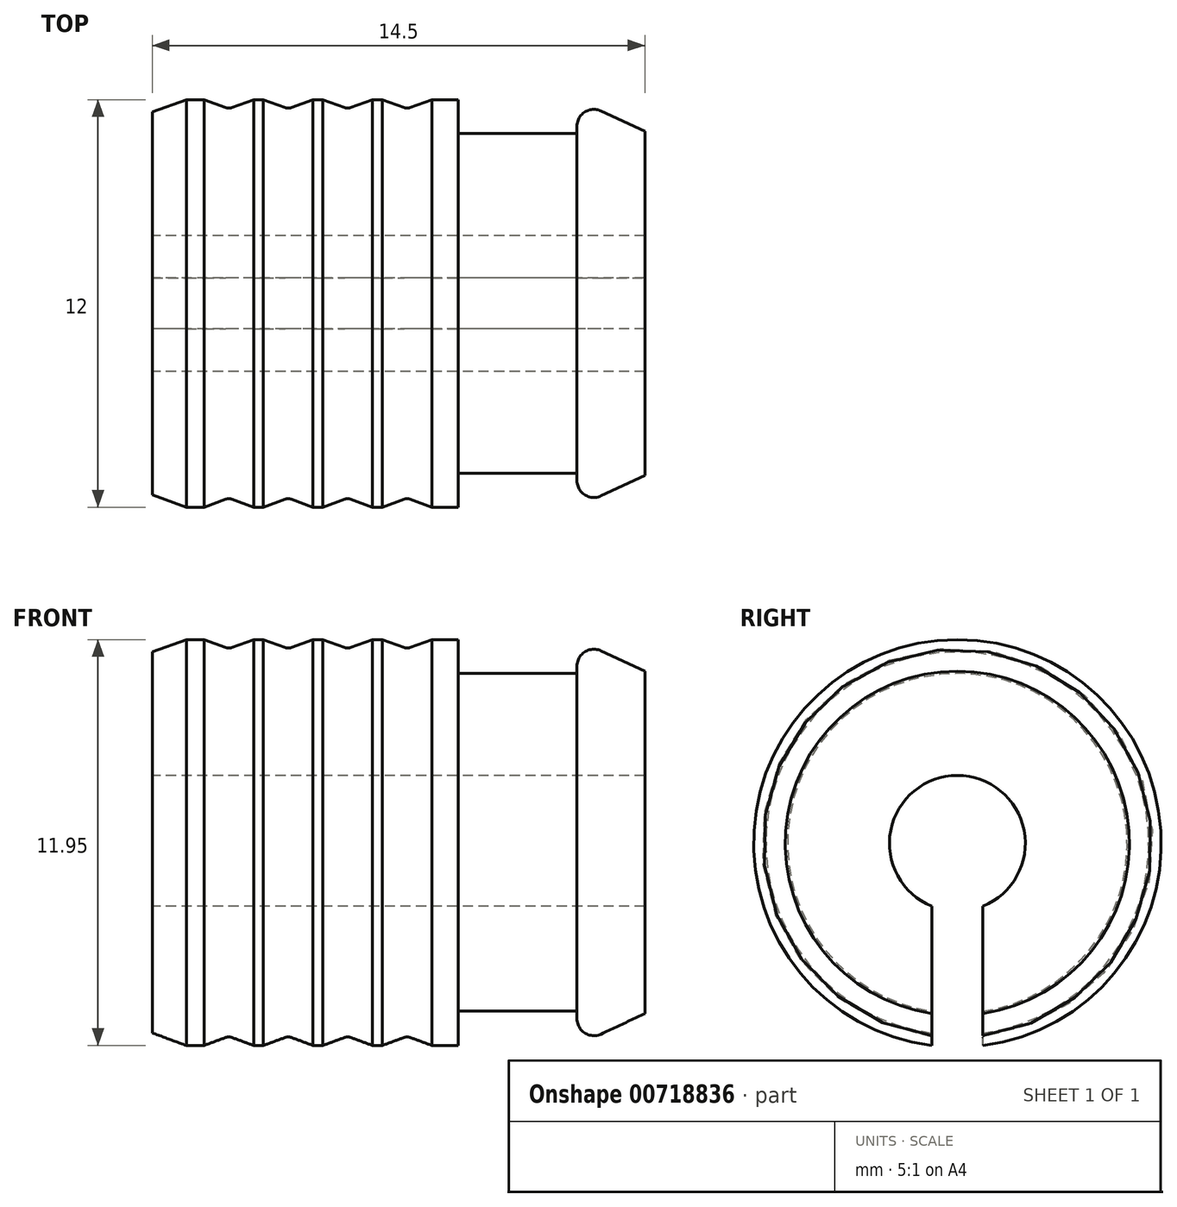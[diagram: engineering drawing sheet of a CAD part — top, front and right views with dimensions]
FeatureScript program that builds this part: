
annotation { "Feature Type Name" : "Feature", "Feature Type Description" : "" }
export const myFeature = defineFeature(function(context is Context, id is Id, definition is map)
    precondition{}
    {
        {
            var Q0;
            Q0=qCreatedBy(makeId("Right.planeOp"),FACE);
            var sketch = newSketch(context, id + "F0", { "sketchPlane" : qUnion([Q0])});
            skLineSegment(sketch, "E0", {"start": v(-0.75, -4.94) * mm, "end": v(-0.75, -1.85) * mm});
            skLineSegment(sketch, "E1.MirrorCS", {"start": v(0.75, -4.94) * mm, "end": v(0.75, -1.85) * mm});
            skArc(sketch, "E2.converted", {"start": v(0.75, -4.94) * mm, "mid": v(0, 5) * mm, "end": v(-0.75, -4.94) * mm});
            skArc(sketch, "E3.converted", {"start": v(0.75, -1.85) * mm, "mid": v(0, 2) * mm, "end": v(-0.75, -1.85) * mm});
            skSolve(sketch);
        }
        {
            var Q0;
            Q0=makeQuery(id+"F0.imprint","IMPRINT",FACE,{"disambiguationData":[TD([[makeQuery(id+"F0.imprint","IMPRINT",EDGE,{"derivedFrom":sQuery(id+"F0.wireOp",EDGE,"rWxJthvj-wXdo-B1tD-YQ2n-WT2CHocByGFI")}),1.0]])]});
            var Q1;
            Q1=makeQuery(id+"F0.imprint","IMPRINT",FACE,{"disambiguationData":[TD([[makeQuery(id+"F0.imprint","IMPRINT",EDGE,{"derivedFrom":sQuery(id+"F0.wireOp",EDGE,"E0")}),1.0]])]});
            extrude(context, id + "F1", {"entities" : qUnion([Q0, Q1]), "depth" : 3.5 * mm, "offsetDistance" : 25 * mm});
        }
        {
            var Q0;
            Q0=makeQuery(id+"F1.opExtrude","CAP_FACE",FACE,{"disambiguationData":[OSD([sQuery(id+"F0.wireOp",EDGE,"rWxJthvj-wXdo-B1tD-YQ2n-WT2CHocByGFI"),sQuery(id+"F0.wireOp",EDGE,"jSeWnfQw-v77B-sO2k-spRN-ma3qYzi9focl"),sQuery(id+"F0.wireOp",EDGE,"E0"),sQuery(id+"F0.wireOp",EDGE,"E1.MirrorCS")])],"isStart":false});
            var sketch = newSketch(context, id + "F2", { "sketchPlane" : qUnion([Q0])});
            skLineSegment(sketch, "E4", {"start": v(-0.75, -2.9) * mm, "end": v(-0.75, -5.95) * mm});
            skLineSegment(sketch, "E5.MirrorCS", {"start": v(0.75, -2.9) * mm, "end": v(0.75, -5.95) * mm});
            skArc(sketch, "E6.converted", {"start": v(0.75, -5.95) * mm, "mid": v(0, 6) * mm, "end": v(-0.75, -5.95) * mm});
            skArc(sketch, "E7.converted", {"start": v(0.75, -2.9) * mm, "mid": v(0, 3) * mm, "end": v(-0.75, -2.9) * mm});
            skSolve(sketch);
        }
        {
            var Q0;
            {var subQ2=sQuery(id+"F2.wireOp",EDGE,"E7.converted");Q0=makeQuery(id+"F2.imprint","IMPRINT",FACE,{"disambiguationData":[TD([[makeQuery(id+"F2.imprint","IMPRINT",EDGE,{"derivedFrom":subQ2}),-1.0]])]});}
            var Q1;
            {var subQ2=sQuery(id+"F2.wireOp",EDGE,"E6.converted");Q1=makeQuery(id+"F2.imprint","IMPRINT",FACE,{"disambiguationData":[TD([[makeQuery(id+"F2.imprint","IMPRINT",EDGE,{"derivedFrom":subQ2}),1.0]])]});}
            extrude(context, id + "F3", {"entities" : qUnion([Q0, Q1]), "operationType" : NewBodyOperationType.ADD, "depth" : 2 * mm, "offsetDistance" : 25 * mm});
        }
        {
            var Q0;
            Q0=makeQuery(id+"F3.opExtrude","CAP_EDGE",EDGE,{"disambiguationData":[OSD([sQuery(id+"F2.wireOp",EDGE,"E6.converted")])],"isStart":false});
            chamfer(context, id + "F4", {"entities" : qUnion([Q0]), "chamferType" : ChamferType.OFFSET_ANGLE, "width" : 2 * mm, "oppositeDirection" : true, "angle" : 25 * degree, "tangentPropagation" : true});
        }
        {
            var Q0;
            {var subQ0=sQuery(id+"F2.wireOp",EDGE,"1d721650-be49-4477-a1dd-ca0bc1895772.0");Q0=makeQuery(id+"F4.opChamfer","BLEND_EDGE",EDGE,{"blendedFrom":[makeQuery(id+"F3.opExtrude","CAP_EDGE",EDGE,{"disambiguationData":[OSD([subQ0])],"isStart":false}),makeQuery(id+"F3.opExtrude","CAP_FACE",FACE,{"disambiguationData":[OSD([subQ0,sQuery(id+"F2.wireOp",EDGE,"411n5QKR-CTX6-nig6-EJTD-6PbGcN82AGl1"),sQuery(id+"F2.wireOp",EDGE,"E4"),sQuery(id+"F2.wireOp",EDGE,"E5.MirrorCS")])],"isStart":true})],"blendedInto":[makeQuery(id+"F3.opExtrude","CAP_FACE",FACE,{"disambiguationData":[OSD([subQ0,sQuery(id+"F2.wireOp",EDGE,"411n5QKR-CTX6-nig6-EJTD-6PbGcN82AGl1"),sQuery(id+"F2.wireOp",EDGE,"E4"),sQuery(id+"F2.wireOp",EDGE,"E5.MirrorCS")])],"isStart":true})]});}
            var Q1;
            {var subQ0=sQuery(id+"F2.wireOp",EDGE,"E6.converted");Q1=makeQuery(id+"F4.opChamfer","BLEND_EDGE",EDGE,{"blendedFrom":[makeQuery(id+"F3.opExtrude","CAP_EDGE",EDGE,{"disambiguationData":[OSD([subQ0])],"isStart":false}),makeQuery(id+"F3.opExtrude","CAP_FACE",FACE,{"disambiguationData":[OSD([sQuery(id+"F2.wireOp",EDGE,"E4"),sQuery(id+"F2.wireOp",EDGE,"E5.MirrorCS"),subQ0,sQuery(id+"F2.wireOp",EDGE,"E7.converted")])],"isStart":true})],"blendedInto":[makeQuery(id+"F3.opExtrude","CAP_FACE",FACE,{"disambiguationData":[OSD([sQuery(id+"F2.wireOp",EDGE,"E4"),sQuery(id+"F2.wireOp",EDGE,"E5.MirrorCS"),subQ0,sQuery(id+"F2.wireOp",EDGE,"E7.converted")])],"isStart":true})]});}
            fillet(context, id + "F5", {"entities" : qUnion([Q0, Q1]), "radius" : 0.5 * mm, "tangentPropagation" : true, "allowEdgeOverflow" : false});
        }
        {
            var Q0;
            Q0=makeQuery(id+"F1.opExtrude","CAP_FACE",FACE,{"disambiguationData":[OSD([sQuery(id+"F0.wireOp",EDGE,"E0"),sQuery(id+"F0.wireOp",EDGE,"E1.MirrorCS"),sQuery(id+"F0.wireOp",EDGE,"E2.converted"),sQuery(id+"F0.wireOp",EDGE,"E3.converted")])],"isStart":true});
            var sketch = newSketch(context, id + "F6", { "sketchPlane" : qUnion([Q0])});
            skArc(sketch, "E8", {"start": v(0.75, -1.85) * mm, "mid": v(0, 2) * mm, "end": v(-0.75, -1.85) * mm});
            skArc(sketch, "E9", {"start": v(0.75, -5.95) * mm, "mid": v(0, 6) * mm, "end": v(-0.75, -5.95) * mm});
            skLineSegment(sketch, "E10", {"start": v(-0.75, -1.85) * mm, "end": v(-0.75, -5.95) * mm});
            skLineSegment(sketch, "E11.MirrorCS", {"start": v(0.75, -1.85) * mm, "end": v(0.75, -5.95) * mm});
            skSolve(sketch);
        }
        {
            var Q0;
            {var subQ0=sQuery(id+"F6.wireOp",EDGE,"E9");Q0=makeQuery(id+"F6.imprint","IMPRINT",FACE,{"disambiguationData":[TD([[makeQuery(id+"F6.imprint","IMPRINT",EDGE,{"derivedFrom":subQ0}),1.0]])]});}
            var Q1;
            {var subQ0=sQuery(id+"F6.wireOp",EDGE,"E8");Q1=makeQuery(id+"F6.imprint","IMPRINT",FACE,{"disambiguationData":[TD([[makeQuery(id+"F6.imprint","IMPRINT",EDGE,{"derivedFrom":subQ0}),1.0]])]});}
            extrude(context, id + "F7", {"entities" : qUnion([Q0, Q1]), "operationType" : NewBodyOperationType.ADD, "depth" : 9 * mm, "offsetDistance" : 25 * mm});
        }
        {
            var Q0;
            Q0=qCreatedBy(makeId("Front.planeOp"),FACE);
            var sketch = newSketch(context, id + "F8", { "sketchPlane" : qUnion([Q0])});
            skArc(sketch, "E12", {"start": v(-1.59, 5.77) * mm, "mid": v(-1.5, 5.75) * mm, "end": v(-1.41, 5.77) * mm});
            skLineSegment(sketch, "E13", {"start": v(-1.41, 5.77) * mm, "end": v(-0.77, 6) * mm});
            skLineSegment(sketch, "E14", {"start": v(-1.59, 5.77) * mm, "end": v(-2.23, 6) * mm});
            skLineSegment(sketch, "E15", {"start": v(-2.23, 6) * mm, "end": v(-0.77, 6) * mm});
            skLineSegment(sketch, "E16.1.0.0", {"start": v(-3.34, 5.77) * mm, "end": v(-3.98, 6) * mm});
            skLineSegment(sketch, "E16.1.0.1", {"start": v(-3.98, 6) * mm, "end": v(-2.52, 6) * mm});
            skLineSegment(sketch, "E16.1.0.2", {"start": v(-3.16, 5.77) * mm, "end": v(-2.52, 6) * mm});
            skArc(sketch, "E16.1.0.3", {"start": v(-3.34, 5.77) * mm, "mid": v(-3.25, 5.75) * mm, "end": v(-3.16, 5.77) * mm});
            skLineSegment(sketch, "E16.2.0.0", {"start": v(-5.09, 5.77) * mm, "end": v(-5.73, 6) * mm});
            skLineSegment(sketch, "E16.2.0.1", {"start": v(-5.73, 6) * mm, "end": v(-4.27, 6) * mm});
            skLineSegment(sketch, "E16.2.0.2", {"start": v(-4.91, 5.77) * mm, "end": v(-4.27, 6) * mm});
            skArc(sketch, "E16.2.0.3", {"start": v(-5.09, 5.77) * mm, "mid": v(-5, 5.75) * mm, "end": v(-4.91, 5.77) * mm});
            skLineSegment(sketch, "E16.direction1", {"start": v(-3.98, 6) * mm, "end": v(-2.23, 6) * mm, "construction": true});
            skLineSegment(sketch, "E17.0.3.0", {"start": v(-6.84, 5.77) * mm, "end": v(-7.48, 6) * mm});
            skLineSegment(sketch, "E17.3.3.0", {"start": v(-7.48, 6) * mm, "end": v(-6.02, 6) * mm});
            skLineSegment(sketch, "E17.6.3.0", {"start": v(-6.66, 5.77) * mm, "end": v(-6.02, 6) * mm});
            skArc(sketch, "E17.9.3.0", {"start": v(-6.84, 5.77) * mm, "mid": v(-6.75, 5.75) * mm, "end": v(-6.66, 5.77) * mm});
            skSolve(sketch);
        }
        {
            var Q0;
            Q0=makeQuery(id+"F8.imprint","IMPRINT",FACE,{"disambiguationData":[TD([[makeQuery(id+"F8.imprint","IMPRINT",EDGE,{"derivedFrom":sQuery(id+"F8.wireOp",EDGE,"E17.0.3.0")}),-1.0]])]});
            var Q1;
            Q1=makeQuery(id+"F8.imprint","IMPRINT",FACE,{"disambiguationData":[TD([[makeQuery(id+"F8.imprint","IMPRINT",EDGE,{"derivedFrom":sQuery(id+"F8.wireOp",EDGE,"E16.2.0.0")}),-1.0]])]});
            var Q2;
            Q2=makeQuery(id+"F8.imprint","IMPRINT",FACE,{"disambiguationData":[TD([[makeQuery(id+"F8.imprint","IMPRINT",EDGE,{"derivedFrom":sQuery(id+"F8.wireOp",EDGE,"E16.1.0.0")}),-1.0]])]});
            var Q3;
            Q3=makeQuery(id+"F8.imprint","IMPRINT",FACE,{"disambiguationData":[TD([[makeQuery(id+"F8.imprint","IMPRINT",EDGE,{"derivedFrom":sQuery(id+"F8.wireOp",EDGE,"E12")}),1.0]])]});
            var Q4;
            Q4=makeQuery(id+"F7.boolean.opBoolean","MERGE",FACE,{"derivedFrom":[makeQuery(id+"F1.opExtrude","SWEPT_FACE",FACE,{"disambiguationData":[OSD([sQuery(id+"F0.wireOp",EDGE,"E3.converted")])]}),makeQuery(id+"F7.opExtrude","SWEPT_FACE",FACE,{"disambiguationData":[OSD([sQuery(id+"F6.wireOp",EDGE,"E8")])]})]});
            revolve(context, id + "F9", {"operationType" : NewBodyOperationType.REMOVE, "surfaceOperationType" : NewSurfaceOperationType.NEW, "entities" : qUnion([Q0, Q1, Q2, Q3]), "axis" : qUnion([Q4]), "revolveType" : RevolveType.FULL, "oppositeDirection" : true});
        }
        {
            var Q0;
            Q0=makeQuery(id+"F7.opExtrude","CAP_EDGE",EDGE,{"disambiguationData":[OSD([sQuery(id+"F6.wireOp",EDGE,"E9")])],"isStart":false});
            chamfer(context, id + "F10", {"entities" : qUnion([Q0]), "chamferType" : ChamferType.OFFSET_ANGLE, "width" : 1 * mm, "oppositeDirection" : true, "angle" : 20 * degree, "tangentPropagation" : true});
        }
        {
            var Q0;
            Q0=makeQuery(id+"F1.opExtrude","CAP_FACE",FACE,{"disambiguationData":[OSD([sQuery(id+"F0.wireOp",EDGE,"E0"),sQuery(id+"F0.wireOp",EDGE,"E1.MirrorCS"),sQuery(id+"F0.wireOp",EDGE,"E2.converted"),sQuery(id+"F0.wireOp",EDGE,"E3.converted")])],"isStart":false});
            var Q1;
            Q1=makeQuery(id+"F3.opExtrude","CAP_FACE",FACE,{"disambiguationData":[OSD([sQuery(id+"F2.wireOp",EDGE,"E4"),sQuery(id+"F2.wireOp",EDGE,"E5.MirrorCS"),sQuery(id+"F2.wireOp",EDGE,"E6.converted"),sQuery(id+"F2.wireOp",EDGE,"E7.converted")])],"isStart":false});
            extrude(context, id + "F11", {"entities" : qUnion([Q0]), "operationType" : NewBodyOperationType.ADD, "endBound" : BoundingType.UP_TO_SURFACE, "depth" : 25 * mm, "endBoundEntityFace" : qUnion([Q1]), "offsetDistance" : 25 * mm});
        }
    });
